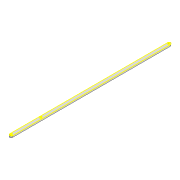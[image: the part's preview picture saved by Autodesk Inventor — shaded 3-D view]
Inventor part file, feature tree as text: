
AUTODESK INVENTOR PART (.ipt)
format: ipt  version: 2022 (Build 260153000, 153)  size: 95,232 bytes
history: native  units: mm
features: sketch x2, extrude x1, projected_geometry x1
ambient origin geometry x8: Origin, YZ Plane, XZ Plane, XY Plane, X Axis, Y Axis, Z Axis, Center Point
bodies: Solid1 (feature_tree)
feature tree (4):
  extrude  "Extrusion1"  Depth=8.0mm
  sketch  "Sketch2"  dims[d2=3.0mm d3=3.0mm d4=4.5mm d5=0.0mm d6=3.0mm d7=334.103mm]
  sketch  "Sketch1"  dims[d0=411.151mm d1=8.0mm]
  projected_geometry  "Projected Loop1"
